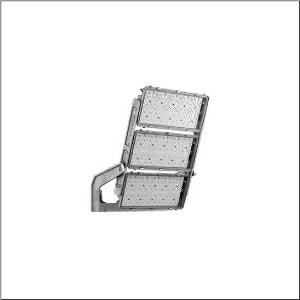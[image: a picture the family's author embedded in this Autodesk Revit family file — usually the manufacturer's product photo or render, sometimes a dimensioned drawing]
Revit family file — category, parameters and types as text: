
# Revit family: floodlight_fl_11_maxi_pro_remote___pl33t_5xa779427t01aa_b0c2
name_source: partatom
category: Lighting Fixtures
units: mm (PartAtom-declared; Revit-internal decimal feet)

## family parameters
Cut with Voids When Loaded = No
Host = Face
Light Source = No
Part Type = Normal
Room Calculation Point = No
Round Connector Dimension = Use Diameter
Shared = No

## types (1)
- --- (1 x LED, 215350 lm, 1540.1 W, 5000K)
    Apparent Load = 1540 VA
    CIE Flux Codes = 27 70 98 100 100
    Color Rendering = 70
    Color Temperature = 5000K
    Default Elevation = 1800 mm
    Description = Floodlight FL 11  maxi  pro Remote floodlight; light control with lens of PMMA; cover panel of toughened safety glass, transparent; light distribution: PL33T, asymmetric direct distribution, LEDcolour temperature: 5000K, rated luminous flux: 215.350lm, colour rendering: CRI > 70, light colour: 750; luminous efficacy: 140lm/W; brightness control: DALI 2 (1 DALI address); with terminal, 8-pole, max. 2.5mm², mains connection: 220..240V/380..400V AC, 50/60Hz, surge voltage resistance: line to ground: 10kV, ECG replaceable separately, no afterglow with DALI off / DMX off command, LED unit replaceable without ESD environment, dustproof LED module, dimming range 10..100%; 1540W floodlight with 2x LED unit of diecast aluminium, coated grey; length: 713mm / width: 651mm / height: 338mm; mounting bracket, of diecast aluminium, uncoated, natural, equipment: Power, protection rating (complete): IP66; insulation class (complete): insulation class I (protective earthing); certification: CE, ENEC, VDE; ball protection: ball impact resistance with accessories, impact resistance: IK07; only for outdoor installations, rated ambient temperature 10°C, permissible operating ambient temperature: -40..+30°C, permissible storage temperature: -40..+85°Cpackaging unit: 1 piece

Light Distribution: PL33T
    Height = 320 mm
    Lamp = 1 x LED
    Lamp Light Flux = 215350 lm
    Lamp Power = 1540.1 W
    Lamp count = 1
    Length = 1002 mm
    Luminous efficacy = 140 lm/W
    Manufacturer = Siteco
    ModVariant = No
    Model = 5XA779427T01AA
    Mounting Place = Ceiling
    Mounting Type = Surface mounted
    Number of Poles = 1
    OnlyDefault = Yes
    Power Factor = 1
    Product Name = Floodlight FL 11 maxi pro Remote | PL33T
    Product group = floodlight | ceiling mounted
    ProductGroupID = 301
    Protection Class = Protection class I
    Protection Degree = IP 66
    RLX_Detail_Level = 1
    RLX_Emergency_Light_Flux = 0 lm
    RLX_Emergency_Type = 0
    RLX_Emergency_Type_DB = No
    RlxData = <blob elided: 52373 chars, md5=4f99b220>
    Socket = socket
    Standby Power = 0 W
    System Light Flux = 215350 lm
    System Power = 1540 W
    Type Comments = factory setting: luminous flux: 100 % | dim-lin: 254 | 1080 mA
    Type Image = l_1349141.jpg
    URL = http://relux.com
    VarID = @adj_079692
    Voltage = 0 V
    Weight = 0.00 kg
    Width = 655 mm

## geometry (parser evidence)
native form markers: Blend x4, Sweep x14
no freeform markers — native parametric forms only
